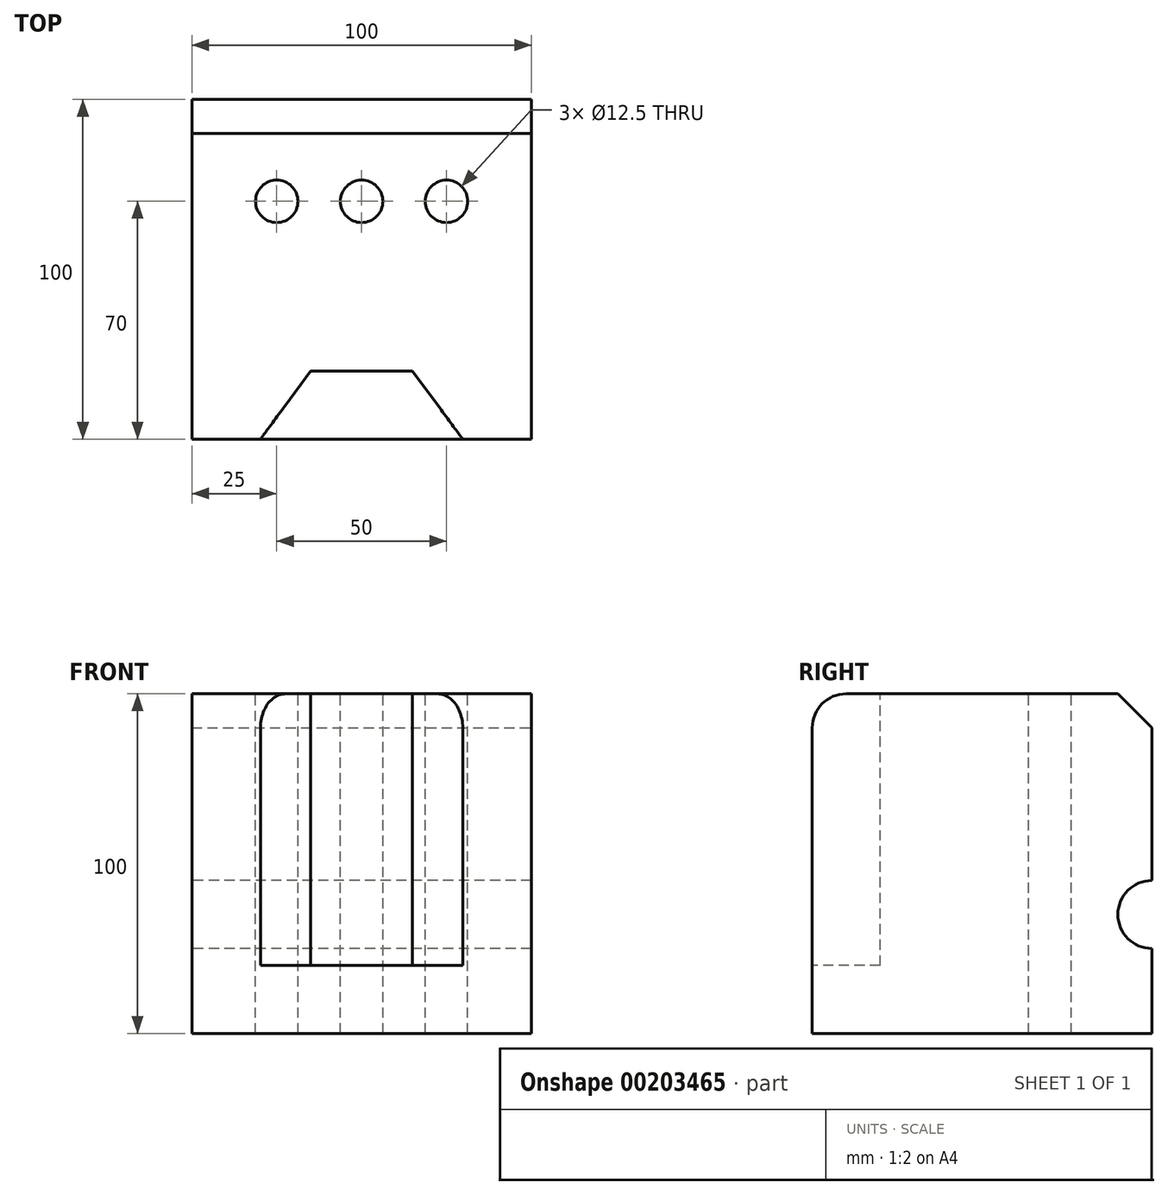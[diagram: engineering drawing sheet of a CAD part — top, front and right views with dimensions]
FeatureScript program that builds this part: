
annotation { "Feature Type Name" : "Feature", "Feature Type Description" : "" }
export const myFeature = defineFeature(function(context is Context, id is Id, definition is map)
    precondition{}
    {
        {
            var Q0;
            Q0=qCreatedBy(makeId("Right.planeOp"),FACE);
            var sketch = newSketch(context, id + "F0", { "sketchPlane" : qUnion([Q0])});
            skLineSegment(sketch, "E0", {"start": v(0, 0) * mm, "end": v(0, 100) * mm});
            skLineSegment(sketch, "E1", {"start": v(0, 100) * mm, "end": v(-90, 100) * mm});
            skLineSegment(sketch, "E2", {"start": v(-100, 90) * mm, "end": v(-100, 0) * mm});
            skLineSegment(sketch, "E3", {"start": v(-100, 0) * mm, "end": v(0, 0) * mm});
            skCircle(sketch, "E4", {"center": v(0, 35) * mm, "radius": 10 * mm});
            skPoint(sketch, "E5.visualSharp", {"position": v(-100, 100) * mm});
            skArc(sketch, "E5.filletArc", {"start": v(-90, 100) * mm, "mid": v(-97.07, 97.07) * mm, "end": v(-100, 90) * mm});
            skSolve(sketch);
        }
        {
            var Q0;
            {var subQ0=sQuery(id+"F0.wireOp",EDGE,"E1");Q0=makeQuery(id+"F0.imprint","IMPRINT",FACE,{"disambiguationData":[TD([[makeQuery(id+"F0.imprint","IMPRINT",EDGE,{"derivedFrom":subQ0}),1.0]])]});}
            extrude(context, id + "F1", {"entities" : qUnion([Q0]), "depth" : 100 * mm});
        }
        {
            var Q0;
            Q0=makeQuery(id+"F1.opExtrude","SWEPT_EDGE",EDGE,{"disambiguationData":[OSD([sQuery(id+"F0.wireOp",EDGE,"E0"),sQuery(id+"F0.wireOp",EDGE,"E1")])]});
            chamfer(context, id + "F2", {"entities" : qUnion([Q0]), "width" : 10 * mm, "tangentPropagation" : true});
        }
        {
            var Q0;
            Q0=makeQuery(id+"F1.opExtrude","SWEPT_FACE",FACE,{"disambiguationData":[OSD([sQuery(id+"F0.wireOp",EDGE,"E1")])]});
            var sketch = newSketch(context, id + "F3", { "sketchPlane" : qUnion([Q0])});
            skCircle(sketch, "E6", {"center": v(25, -30) * mm, "radius": 6.25 * mm});
            skCircle(sketch, "E7", {"center": v(50, -30) * mm, "radius": 6.25 * mm});
            skCircle(sketch, "E8", {"center": v(75, -30) * mm, "radius": 6.25 * mm});
            skSolve(sketch);
        }
        {
            var Q0;
            Q0 = qSketchRegion(id + "F3", true);
            extrude(context, id + "F4", {"entities" : qUnion([Q0]), "operationType" : NewBodyOperationType.REMOVE, "oppositeDirection" : true, "depth" : 100 * mm});
        }
        {
            var Q0;
            Q0=makeQuery(id+"F1.opExtrude","SWEPT_FACE",FACE,{"disambiguationData":[OSD([sQuery(id+"F0.wireOp",EDGE,"E1")])]});
            var sketch = newSketch(context, id + "F5", { "sketchPlane" : qUnion([Q0])});
            skLineSegment(sketch, "E9", {"start": v(35, -80) * mm, "end": v(65, -80) * mm});
            skLineSegment(sketch, "E10", {"start": v(35, -80) * mm, "end": v(20, -100.3) * mm});
            skLineSegment(sketch, "E11", {"start": v(20, -100.3) * mm, "end": v(80, -100.3) * mm});
            skLineSegment(sketch, "E12", {"start": v(65, -80) * mm, "end": v(80, -100.3) * mm});
            skPoint(sketch, "E13.endSnap0", {"position": v(50, -10) * mm});
            skSolve(sketch);
        }
        {
            var Q0;
            Q0 = qSketchRegion(id + "F5", true);
            extrude(context, id + "F6", {"entities" : qUnion([Q0]), "operationType" : NewBodyOperationType.REMOVE, "oppositeDirection" : true, "depth" : 80 * mm});
        }
    });
